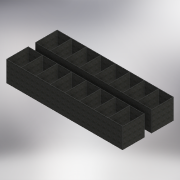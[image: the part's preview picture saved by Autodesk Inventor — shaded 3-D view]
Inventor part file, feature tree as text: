
AUTODESK INVENTOR PART (.ipt)
format: ipt  version: 2016 (Build 200138000, 138)  size: 361,984 bytes
history: native  units: mm
features: extrude x24, sketch x6, other x1
ambient origin geometry x8: Origin, YZ Plane, XZ Plane, XY Plane, X Axis, Y Axis, Z Axis, Center Point
bodies: Body1 (feature_tree)
feature tree (31):
  other  "Sólido1"
  extrude  "Extrusión1"  Depth=700.0mm TaperAngle=0.0deg
  sketch  "Boceto2"  dims[d4=700.0mm d5=0.0mm d6=700.0mm d7=0.0mm]
  extrude  "Extrusión2"  Depth=700.0mm TaperAngle=0.0deg
  extrude  "Extrusión3"  Depth=700.0mm TaperAngle=0.0deg
  extrude  "Extrusión4"  Depth=700.0mm TaperAngle=0.0deg
  extrude  "Extrusión5"  Depth=700.0mm TaperAngle=0.0deg
  extrude  "Extrusión6"  Depth=700.0mm TaperAngle=0.0deg
  extrude  "Extrusión7"  Depth=10.0mm TaperAngle=0.0deg
  extrude  "Extrusión8"  Depth=700.0mm TaperAngle=0.0deg
  extrude  "Extrusión9"  Depth=700.0mm TaperAngle=0.0deg
  extrude  "Extrusión10"  Depth=700.0mm TaperAngle=0.0deg
  sketch  "Boceto3"  dims[d8=700.0mm d9=0.0mm d10=700.0mm d11=0.0mm]
  extrude  "Extrusión11"  Depth=700.0mm TaperAngle=0.0deg
  extrude  "Extrusión12"  Depth=700.0mm TaperAngle=0.0deg
  extrude  "Extrusión13"  Depth=700.0mm TaperAngle=0.0deg
  sketch  "Boceto5"  dims[d16=700.0mm d17=0.0mm d18=700.0mm d19=0.0mm]
  extrude  "Extrusión14"  Depth=700.0mm TaperAngle=0.0deg
  extrude  "Extrusión15"  Depth=700.0mm TaperAngle=0.0deg
  extrude  "Extrusión16"  Depth=700.0mm TaperAngle=0.0deg
  extrude  "Extrusión17"  Depth=700.0mm TaperAngle=0.0deg
  extrude  "Extrusión18"  Depth=700.0mm TaperAngle=0.0deg
  extrude  "Extrusión19"  [1 undecoded]
  extrude  "Extrusión20"  [1 undecoded]
  extrude  "Extrusión21"  [1 undecoded]
  extrude  "Extrusión22"  [1 undecoded]
  sketch  "Boceto6"  dims[d20=700.0mm d21=0.0mm d22=700.0mm d23=0.0mm d24=10.0mm d25=0.0mm d26=700.0mm d27=0.0mm d28=700.0mm d29=0.0mm d30=700.0mm d31=0.0mm d32=700.0mm d33=0.0mm d34=700.0mm d35=0.0mm d36=700.0mm d37=0.0mm d38=700.0mm d39=0.0mm d40=700.0mm d41=0.0mm d42=700.0mm d43=0.0mm d44=700.0mm d45=0.0mm d46=700.0mm d47=0.0mm]
  extrude  "Extrusión23"  [1 undecoded]
  extrude  "Extrusión24"  [1 undecoded]
  sketch  "Boceto1"  dims[d0=10.0mm d1=0.0mm d2=700.0mm d3=0.0mm]
  sketch  "Boceto4"  dims[d12=700.0mm d13=0.0mm d14=700.0mm d15=0.0mm]
note: 6 required parameter values undecoded (feature->parameter linkage not recoverable at this tier; creation-order binding heuristic only, values carry confidence <= 0.55)
